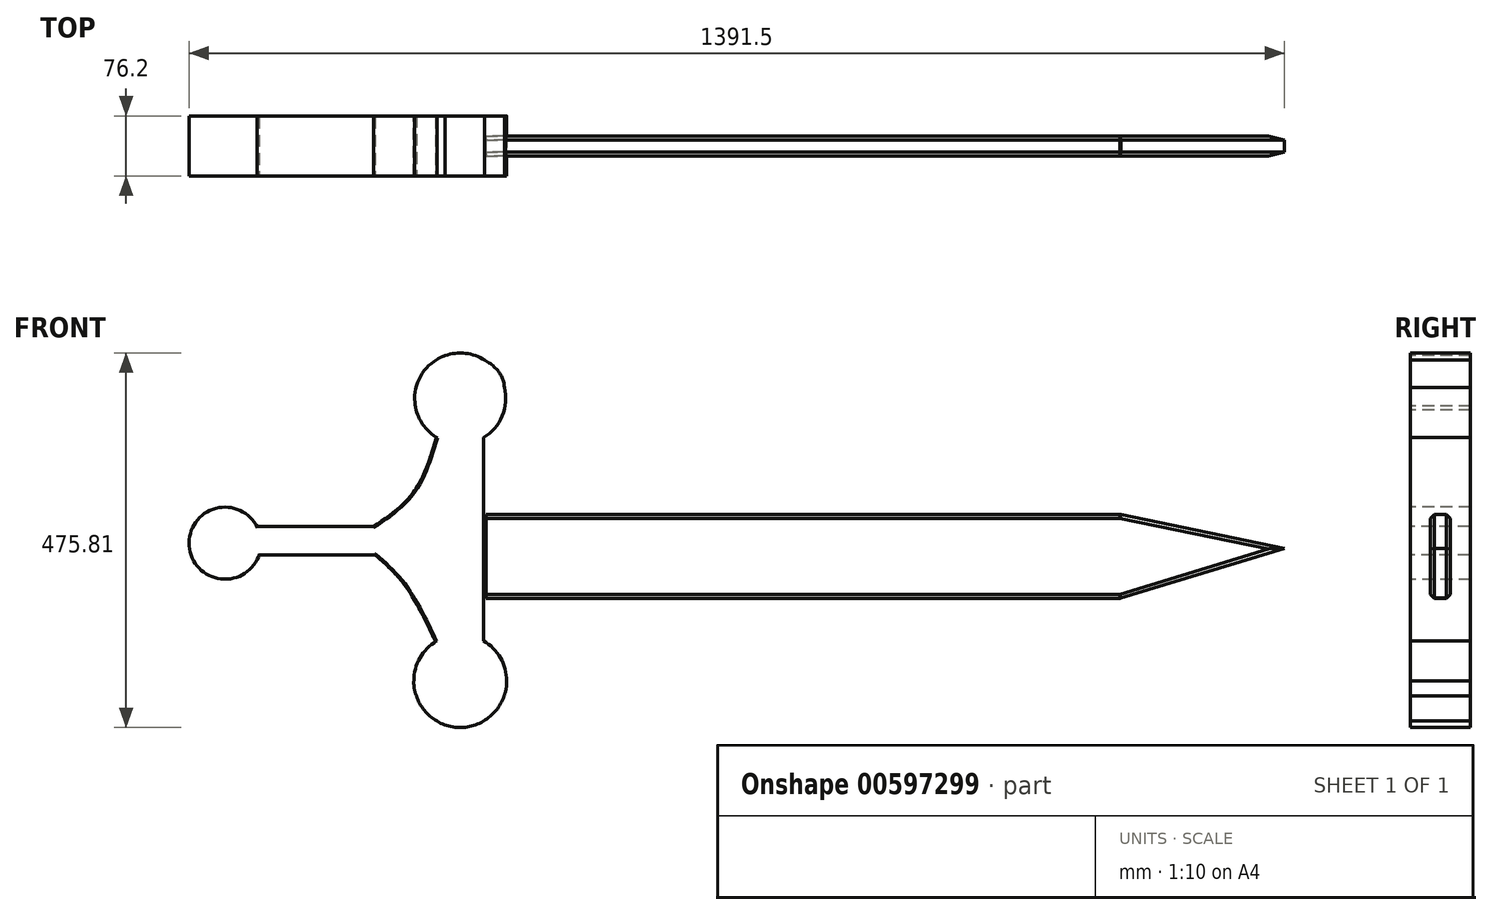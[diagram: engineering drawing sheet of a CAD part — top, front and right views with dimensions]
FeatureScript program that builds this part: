
annotation { "Feature Type Name" : "Feature", "Feature Type Description" : "" }
export const myFeature = defineFeature(function(context is Context, id is Id, definition is map)
    precondition{}
    {
        {
            var Q0;
            Q0=qCreatedBy(makeId("Front.planeOp"),FACE);
            var sketch = newSketch(context, id + "F0", { "sketchPlane" : qUnion([Q0])});
            skCircle(sketch, "E0", {"center": v(-520.06, 54.91) * mm, "radius": 45.77 * mm});
            skLineSegment(sketch, "E1.bottom", {"start": v(-479.43, 75.97) * mm, "end": v(-250.83, 75.97) * mm});
            skLineSegment(sketch, "E1.top", {"start": v(-479.43, 40.16) * mm, "end": v(-250.83, 40.16) * mm});
            skLineSegment(sketch, "E1.left", {"start": v(-479.43, 75.97) * mm, "end": v(-479.43, 40.16) * mm});
            skLineSegment(sketch, "E1.right", {"start": v(-250.83, 75.97) * mm, "end": v(-250.83, 40.16) * mm});
            skLineSegment(sketch, "E2.bottom", {"start": v(-250.83, 191.37) * mm, "end": v(-191.82, 191.37) * mm});
            skLineSegment(sketch, "E2.top", {"start": v(-250.83, -74.17) * mm, "end": v(-191.82, -74.17) * mm});
            skLineSegment(sketch, "E2.left", {"start": v(-250.83, 191.37) * mm, "end": v(-250.83, -74.17) * mm});
            skLineSegment(sketch, "E2.right", {"start": v(-191.82, 191.37) * mm, "end": v(-191.82, -74.17) * mm});
            skCircle(sketch, "E3", {"center": v(-221.33, 238.62) * mm, "radius": 57.83 * mm});
            skPoint(sketch, "E3.centerSnap0", {"position": v(-221.33, 191.37) * mm});
            skCircle(sketch, "E4", {"center": v(-221.33, -120.11) * mm, "radius": 58.95 * mm});
            skPoint(sketch, "E4.centerSnap0", {"position": v(-221.33, -74.17) * mm});
            skLineSegment(sketch, "E5.left", {"start": v(-191.82, 40.16) * mm, "end": v(-191.82, 75.97) * mm});
            skFitSpline(sketch, "E6", {"points": [v(-250.83, 191.37) * mm, v(-278.4, 229.28) * mm, v(-250.83, 288.36) * mm, v(-190.15, 287.33) * mm, v(-165.26, 252.79) * mm, v(-191.82, 191.37) * mm], "startDerivative": vector(-209.38, 174.42) * mm, "endDerivative": vector(-186.82, -297.22) * mm});
            skFitSpline(sketch, "E7", {"points": [v(-250.83, -74.17) * mm, v(-280.28, -120.11) * mm, v(-250.83, -171.15) * mm, v(-191.82, -171.15) * mm, v(-162.37, -120.11) * mm, v(-191.82, -74.17) * mm], "startDerivative": vector(-217, -217.94) * mm, "endDerivative": vector(-217, 217.94) * mm});
            skFitSpline(sketch, "E8", {"points": [v(-250.83, 191.37) * mm, v(-280.26, 120.11) * mm, v(-331.5, 75.97) * mm], "startDerivative": vector(-44.35, -150.07) * mm, "endDerivative": vector(-117.8, -79.96) * mm});
            skFitSpline(sketch, "E9", {"points": [v(-250.83, -74.17) * mm, v(-290.6, 0) * mm, v(-329.49, 40.16) * mm], "startDerivative": vector(-68.19, 147.08) * mm, "endDerivative": vector(-89.86, 79.28) * mm});
            skSolve(sketch);
        }
        {
            var Q0;
            Q0 = qSketchRegion(id + "F0", true);
            extrude(context, id + "F1", {"entities" : qUnion([Q0]), "endBound" : BoundingType.SYMMETRIC, "oppositeDirection" : true, "depth" : 76.2 * mm, "offsetDistance" : 25.4 * mm});
        }
        {
            var Q0;
            Q0=makeQuery(id+"F1.opExtrude","CAP_EDGE",EDGE,{"disambiguationData":[OSD([sQuery(id+"F0.wireOp",EDGE,"E1.bottom")])],"isStart":true});
            var Q1;
            Q1=makeQuery(id+"F1.opExtrude","CAP_EDGE",EDGE,{"disambiguationData":[OSD([sQuery(id+"F0.wireOp",EDGE,"E1.bottom")])],"isStart":false});
            var Q2;
            Q2=makeQuery(id+"F1.opExtrude","CAP_EDGE",EDGE,{"disambiguationData":[OSD([sQuery(id+"F0.wireOp",EDGE,"E1.top")])],"isStart":false});
            var Q3;
            Q3=makeQuery(id+"F1.opExtrude","CAP_EDGE",EDGE,{"disambiguationData":[OSD([sQuery(id+"F0.wireOp",EDGE,"E1.top")])],"isStart":true});
            fillet(context, id + "F2", {"entities" : qUnion([Q0, Q1, Q2, Q3]), "radius" : 1.27 * mm, "tangentPropagation" : true, "allowEdgeOverflow" : false});
        }
        {
            var Q0;
            Q0=makeQuery(id+"F1.opExtrude","CAP_EDGE",EDGE,{"disambiguationData":[OSD([sQuery(id+"F0.wireOp",EDGE,"E9")])],"isStart":true});
            var Q1;
            Q1=makeQuery(id+"F1.opExtrude","CAP_EDGE",EDGE,{"disambiguationData":[OSD([sQuery(id+"F0.wireOp",EDGE,"E8")])],"isStart":true});
            var Q2;
            Q2=makeQuery(id+"F1.opExtrude","CAP_EDGE",EDGE,{"disambiguationData":[OSD([sQuery(id+"F0.wireOp",EDGE,"E8")])],"isStart":false});
            var Q3;
            Q3=makeQuery(id+"F1.opExtrude","CAP_EDGE",EDGE,{"disambiguationData":[OSD([sQuery(id+"F0.wireOp",EDGE,"E9")])],"isStart":false});
            fillet(context, id + "F3", {"entities" : qUnion([Q0, Q1, Q2, Q3]), "radius" : 1.27 * mm, "tangentPropagation" : true, "allowEdgeOverflow" : false});
        }
        {
            var Q0;
            Q0=qCreatedBy(makeId("Front.planeOp"),FACE);
            var sketch = newSketch(context, id + "F4", { "sketchPlane" : qUnion([Q0])});
            skLineSegment(sketch, "E10.left", {"start": v(-188.76, 0) * mm, "end": v(-188.76, 91.23) * mm});
            skPoint(sketch, "E10.middle", {"position": v(32.09, 45.61) * mm});
            skLineSegment(sketch, "E11.bottom", {"start": v(-188.76, 91.23) * mm, "end": v(617.33, 91.23) * mm});
            skLineSegment(sketch, "E11.top", {"start": v(-188.76, -15.01) * mm, "end": v(617.33, -15.01) * mm});
            skLineSegment(sketch, "E11.left", {"start": v(-188.76, 91.23) * mm, "end": v(-188.76, -15.01) * mm});
            skLineSegment(sketch, "E11.right", {"start": v(617.33, 91.23) * mm, "end": v(617.33, -15.01) * mm});
            skPoint(sketch, "E11.middle", {"position": v(214.29, 38.1) * mm});
            skLineSegment(sketch, "E12", {"start": v(617.33, -15.01) * mm, "end": v(825.67, 48.45) * mm});
            skLineSegment(sketch, "E13", {"start": v(825.67, 48.45) * mm, "end": v(617.33, 91.23) * mm});
            skSolve(sketch);
        }
        {
            var Q0;
            {var subQ0=sQuery(id+"F4.wireOp",EDGE,"E11.bottom");Q0=makeQuery(id+"F4.imprint","IMPRINT",FACE,{"disambiguationData":[TD([[makeQuery(id+"F4.imprint","IMPRINT",EDGE,{"derivedFrom":subQ0}),-1.0]])]});}
            var Q1;
            Q1=makeQuery(id+"F4.imprint","IMPRINT",FACE,{"disambiguationData":[TD([[makeQuery(id+"F4.imprint","IMPRINT",EDGE,{"derivedFrom":sQuery(id+"F4.wireOp",EDGE,"E11.right")}),1.0]])]});
            extrude(context, id + "F5", {"entities" : qUnion([Q0, Q1]), "endBound" : BoundingType.SYMMETRIC, "depth" : 25.4 * mm, "offsetDistance" : 25.4 * mm});
        }
        {
            var Q0;
            Q0=makeQuery(id+"F5.opExtrude","CAP_EDGE",EDGE,{"disambiguationData":[OSD([sQuery(id+"F4.wireOp",EDGE,"E11.bottom")])],"isStart":true});
            var Q1;
            Q1=makeQuery(id+"F5.opExtrude","CAP_EDGE",EDGE,{"disambiguationData":[OSD([sQuery(id+"F4.wireOp",EDGE,"E11.top")])],"isStart":true});
            var Q2;
            Q2=makeQuery(id+"F5.opExtrude","CAP_EDGE",EDGE,{"disambiguationData":[OSD([sQuery(id+"F4.wireOp",EDGE,"E11.top")])],"isStart":false});
            var Q3;
            Q3=makeQuery(id+"F5.opExtrude","CAP_EDGE",EDGE,{"disambiguationData":[OSD([sQuery(id+"F4.wireOp",EDGE,"E11.bottom")])],"isStart":false});
            var Q4;
            Q4=makeQuery(id+"F5.opExtrude","CAP_EDGE",EDGE,{"disambiguationData":[OSD([sQuery(id+"F4.wireOp",EDGE,"E12")])],"isStart":false});
            var Q5;
            Q5=makeQuery(id+"F5.opExtrude","CAP_EDGE",EDGE,{"disambiguationData":[OSD([sQuery(id+"F4.wireOp",EDGE,"E13")])],"isStart":false});
            var Q6;
            Q6=makeQuery(id+"F5.opExtrude","CAP_EDGE",EDGE,{"disambiguationData":[OSD([sQuery(id+"F4.wireOp",EDGE,"E13")])],"isStart":true});
            var Q7;
            Q7=makeQuery(id+"F5.opExtrude","CAP_EDGE",EDGE,{"disambiguationData":[OSD([sQuery(id+"F4.wireOp",EDGE,"E12")])],"isStart":true});
            var Q8;
            Q8=makeQuery(id+"F5.opExtrude","SWEPT_EDGE",EDGE,{"disambiguationData":[OSD([sQuery(id+"F4.wireOp",EDGE,"E11.bottom"),sQuery(id+"F4.wireOp",EDGE,"E11.right"),sQuery(id+"F4.wireOp",EDGE,"E13")])]});
            var Q9;
            Q9=makeQuery(id+"F5.opExtrude","SWEPT_EDGE",EDGE,{"disambiguationData":[OSD([sQuery(id+"F4.wireOp",EDGE,"E11.top"),sQuery(id+"F4.wireOp",EDGE,"E11.right"),sQuery(id+"F4.wireOp",EDGE,"E12")])]});
            chamfer(context, id + "F6", {"entities" : qUnion([Q0, Q1, Q2, Q3, Q4, Q5, Q6, Q7, Q8, Q9]), "width" : 5.08 * mm, "tangentPropagation" : true});
        }
    });
